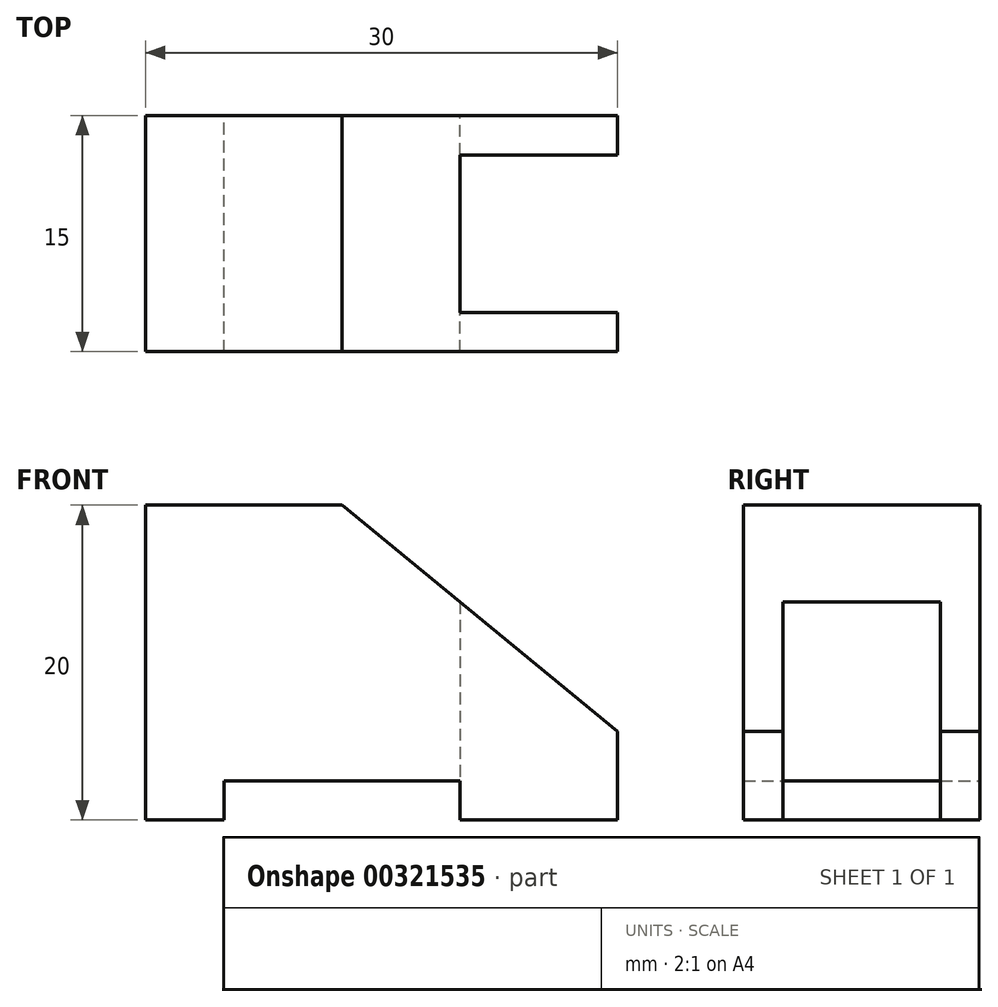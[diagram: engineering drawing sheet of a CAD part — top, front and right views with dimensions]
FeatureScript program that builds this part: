
annotation { "Feature Type Name" : "Feature", "Feature Type Description" : "" }
export const myFeature = defineFeature(function(context is Context, id is Id, definition is map)
    precondition{}
    {
        {
            var Q0;
            Q0=qCreatedBy(makeId("Front.planeOp"),FACE);
            var sketch = newSketch(context, id + "F0", { "sketchPlane" : qUnion([Q0])});
            skLineSegment(sketch, "E0", {"start": v(0, 0) * mm, "end": v(0, 20) * mm});
            skLineSegment(sketch, "E1", {"start": v(0, 20) * mm, "end": v(12.5, 20) * mm});
            skLineSegment(sketch, "E2", {"start": v(12.5, 20) * mm, "end": v(30, 5.64) * mm});
            skLineSegment(sketch, "E3", {"start": v(30, 5.64) * mm, "end": v(30, 0) * mm});
            skLineSegment(sketch, "E4", {"start": v(30, 0) * mm, "end": v(20, 0) * mm});
            skLineSegment(sketch, "E5", {"start": v(20, 0) * mm, "end": v(20, 2.5) * mm});
            skLineSegment(sketch, "E6", {"start": v(20, 2.5) * mm, "end": v(5, 2.5) * mm});
            skLineSegment(sketch, "E7", {"start": v(5, 2.5) * mm, "end": v(5, 0) * mm});
            skLineSegment(sketch, "E8", {"start": v(5, 0) * mm, "end": v(0, 0) * mm});
            skSolve(sketch);
        }
        {
            var Q0;
            Q0 = qSketchRegion(id + "F0", true);
            extrude(context, id + "F1", {"entities" : qUnion([Q0]), "endBound" : BoundingType.SYMMETRIC, "depth" : 15 * mm});
        }
        {
            var Q0;
            Q0=makeQuery(id+"F1.opExtrude","SWEPT_FACE",FACE,{"disambiguationData":[OSD([sQuery(id+"F0.wireOp",EDGE,"E4")])]});
            var sketch = newSketch(context, id + "F2", { "sketchPlane" : qUnion([Q0])});
            skLineSegment(sketch, "E9.bottom", {"start": v(20, 5) * mm, "end": v(55.46, 5) * mm});
            skLineSegment(sketch, "E9.top", {"start": v(20, -5) * mm, "end": v(55.46, -5) * mm});
            skLineSegment(sketch, "E9.left", {"start": v(20, 5) * mm, "end": v(20, -5) * mm});
            skLineSegment(sketch, "E9.right", {"start": v(55.46, 5) * mm, "end": v(55.46, -5) * mm});
            skSolve(sketch);
        }
        {
            var Q0;
            Q0 = qSketchRegion(id + "F2", true);
            extrude(context, id + "F3", {"entities" : qUnion([Q0]), "operationType" : NewBodyOperationType.REMOVE, "endBound" : BoundingType.THROUGH_ALL, "oppositeDirection" : true, "depth" : 25 * mm});
        }
    });
